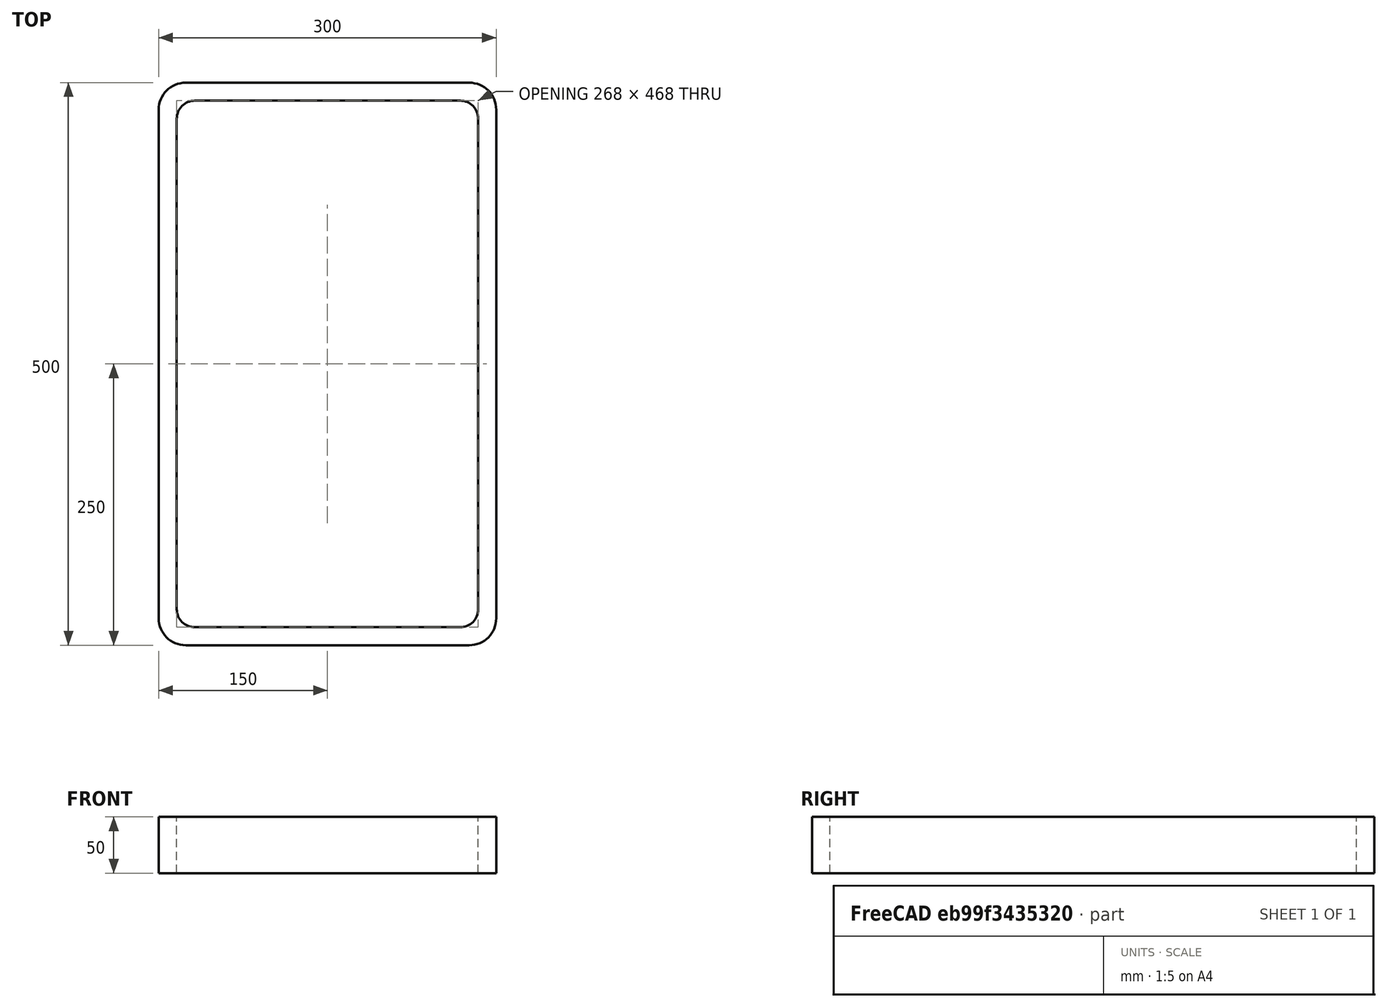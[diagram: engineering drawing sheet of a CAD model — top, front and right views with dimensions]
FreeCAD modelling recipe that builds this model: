
FCSTD DOCUMENT  (FreeCAD 0.15R4671 (Git))
Label: Rectangular hollow section 500x300x16 EN10219 S235JRH
License: All rights reserved
LicenseURL: http://en.wikipedia.org/wiki/All_rights_reserved
objects: Sketcher::SketchObject×1, Part::Extrusion×1
note: 2 computed .brp shape members not serialized (recipe doc carries the construction recipe); baked Part::Feature solids carry a one-line shape summary decoded from their .brp

FEATURE [Sketcher::SketchObject] Sketch
  sketch-geometry (16):
    g0: LineSegment StartX=-118 StartY=234 StartZ=0 EndX=118 EndY=234 EndZ=0
    g1: LineSegment StartX=134 StartY=218 StartZ=0 EndX=134 EndY=-218 EndZ=0
    g2: LineSegment StartX=118 StartY=-234 StartZ=0 EndX=-118 EndY=-234 EndZ=0
    g3: LineSegment StartX=-134 StartY=-218 StartZ=0 EndX=-134 EndY=218 EndZ=0
    g4: LineSegment StartX=-126 StartY=250 StartZ=0 EndX=126 EndY=250 EndZ=0
    g5: LineSegment StartX=150 StartY=226 StartZ=0 EndX=150 EndY=-226 EndZ=0
    g6: LineSegment StartX=126 StartY=-250 StartZ=0 EndX=-126 EndY=-250 EndZ=0
    g7: LineSegment StartX=-150 StartY=-226 StartZ=0 EndX=-150 EndY=226 EndZ=0
    g8: ArcOfCircle CenterX=-118 CenterY=218 CenterZ=0 NormalX=0 NormalY=0 NormalZ=1 Radius=16 StartAngle=1.5708 EndAngle=3.14159
    g9: ArcOfCircle CenterX=118 CenterY=218 CenterZ=0 NormalX=0 NormalY=0 NormalZ=1 Radius=16 StartAngle=0 EndAngle=1.5708
    g10: ArcOfCircle CenterX=118 CenterY=-218 CenterZ=0 NormalX=0 NormalY=0 NormalZ=1 Radius=16 StartAngle=4.71239 EndAngle=6.28319
    g11: ArcOfCircle CenterX=-118 CenterY=-218 CenterZ=0 NormalX=0 NormalY=0 NormalZ=1 Radius=16 StartAngle=3.14159 EndAngle=4.71239
    g12: ArcOfCircle CenterX=126 CenterY=226 CenterZ=0 NormalX=0 NormalY=0 NormalZ=1 Radius=24 StartAngle=0 EndAngle=1.5708
    g13: ArcOfCircle CenterX=126 CenterY=-226 CenterZ=0 NormalX=0 NormalY=0 NormalZ=1 Radius=24 StartAngle=4.71239 EndAngle=6.28319
    g14: ArcOfCircle CenterX=-126 CenterY=-226 CenterZ=0 NormalX=0 NormalY=0 NormalZ=1 Radius=24 StartAngle=3.14159 EndAngle=4.71239
    g15: ArcOfCircle CenterX=-126 CenterY=226 CenterZ=0 NormalX=0 NormalY=0 NormalZ=1 Radius=24 StartAngle=1.5708 EndAngle=3.14159
  constraints (36):
    c: Horizontal(g2)
    c: Vertical(g3)
    c: Horizontal(g6)
    c: Vertical(g7)
    c: Tangent(g3,g8) = 1.5708
    c: Tangent(g0,g8) = 1.5708
    c: Tangent(g0,g9) = 1.5708
    c: Tangent(g1,g9) = 1.5708
    c: Tangent(g1,g10) = 1.5708
    c: Tangent(g2,g10) = 1.5708
    c: Tangent(g2,g11) = 1.5708
    c: Tangent(g3,g11) = 1.5708
    c: Tangent(g4,g12) = 1.5708
    c: Tangent(g5,g12) = 1.5708
    c: Tangent(g5,g13) = 1.5708
    c: Tangent(g6,g13) = 1.5708
    c: Tangent(g6,g14) = 1.5708
    c: Tangent(g7,g14) = 1.5708
    c: Tangent(g7,g15) = 1.5708
    c: Tangent(g4,g15) = 1.5708
    c: Equal(g9,g8)
    c: Equal(g9,g11)
    c: Equal(g9,g10)
    c: Equal(g12,g15)
    c: Equal(g12,g14)
    c: Equal(g12,g13)
    c: Symmetric(g4,g6,g-1)
    c: Symmetric(g7,g5,g-2)
    c: DistanceY(g4,g6) = -500
    c: DistanceX(g7,g5) = 300
    c: Symmetric(g3,g1,g-2)
    c: Symmetric(g0,g2,g-1)
    c: DistanceY(g0,g4) = 16
    c: DistanceX(g5,g1) = -16
    c: Radius(g9) = 16
    c: Radius(g12) = 24
FEATURE [Part::Extrusion] Extrude  label="Rectangular hollow section 500x300x16 EN10219 S235JRH"
  Base = -> Sketch
  Dir = (0,0,50)
  Solid = true
